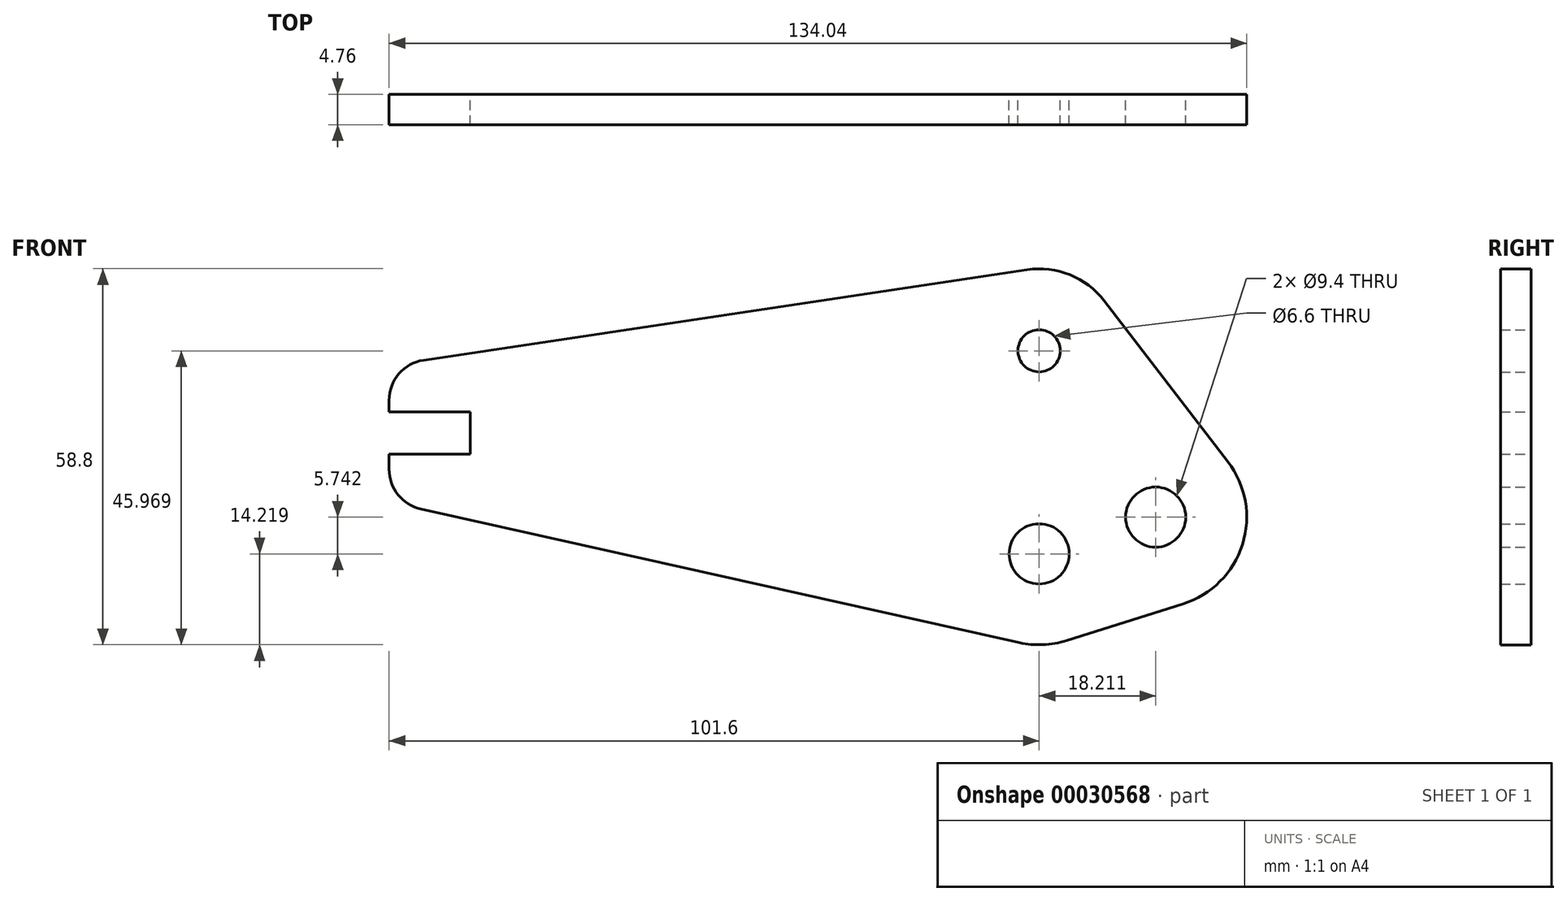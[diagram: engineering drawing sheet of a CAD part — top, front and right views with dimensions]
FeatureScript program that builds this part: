
annotation { "Feature Type Name" : "Feature", "Feature Type Description" : "" }
export const myFeature = defineFeature(function(context is Context, id is Id, definition is map)
    precondition{}
    {
        {
            var Q0;
            Q0=qCreatedBy(makeId("Front.planeOp"),FACE);
            var sketch = newSketch(context, id + "F0", { "sketchPlane" : qUnion([Q0])});
            skLineSegment(sketch, "E0", {"start": v(0, 10.3) * mm, "end": v(0, 12.7) * mm});
            skLineSegment(sketch, "E1", {"start": v(0, 12.7) * mm, "end": v(12.7, 12.7) * mm});
            skLineSegment(sketch, "E2", {"start": v(12.7, 12.7) * mm, "end": v(12.7, 19.3) * mm});
            skLineSegment(sketch, "E3", {"start": v(12.7, 19.3) * mm, "end": v(0, 19.3) * mm});
            skCircle(sketch, "E4", {"center": v(101.6, 28.83) * mm, "radius": 3.3 * mm});
            skArc(sketch, "E5.0", {"start": v(111.77, 36.64) * mm, "mid": v(106.4, 40.72) * mm, "end": v(99.7, 41.51) * mm});
            skLineSegment(sketch, "E6", {"start": v(0, 19.3) * mm, "end": v(0, 21.08) * mm});
            skLineSegment(sketch, "E7", {"start": v(5.4, 27.36) * mm, "end": v(99.7, 41.51) * mm});
            skLineSegment(sketch, "E8", {"start": v(101.6, 28.83) * mm, "end": v(101.6, -2.92) * mm, "construction": true});
            skLineSegment(sketch, "E9", {"start": v(101.6, 28.83) * mm, "end": v(119.81, 2.82) * mm, "construction": true});
            skCircle(sketch, "E10", {"center": v(101.6, -2.92) * mm, "radius": 4.7 * mm});
            skCircle(sketch, "E11", {"center": v(119.81, 2.82) * mm, "radius": 4.7 * mm});
            skArc(sketch, "E12.0", {"start": v(98.5, -16.8) * mm, "mid": v(102.2, -17.13) * mm, "end": v(105.88, -16.49) * mm});
            skArc(sketch, "E13.0", {"start": v(124.09, -10.74) * mm, "mid": v(133.38, -1.45) * mm, "end": v(131.1, 11.48) * mm});
            skLineSegment(sketch, "E14", {"start": v(4.97, 4.1) * mm, "end": v(98.5, -16.8) * mm});
            skLineSegment(sketch, "E15", {"start": v(111.77, 36.64) * mm, "end": v(131.1, 11.48) * mm});
            skLineSegment(sketch, "E16", {"start": v(105.88, -16.49) * mm, "end": v(124.09, -10.74) * mm});
            skArc(sketch, "E17.trimOffspring", {"start": v(96.91, -2.57) * mm, "mid": v(111.15, -1.45) * mm, "end": v(123.45, 5.8) * mm, "construction": true});
            skPoint(sketch, "E18.visualSharp", {"position": v(0, 26.55) * mm});
            skArc(sketch, "E18.filletArc", {"start": v(5.4, 27.36) * mm, "mid": v(1.54, 25.23) * mm, "end": v(0, 21.08) * mm});
            skPoint(sketch, "E19.visualSharp", {"position": v(0, 5.2) * mm});
            skArc(sketch, "E19.filletArc", {"start": v(0, 10.3) * mm, "mid": v(1.4, 6.32) * mm, "end": v(4.97, 4.1) * mm});
            skSolve(sketch);
        }
        {
            var Q0;
            Q0=makeQuery(id+"F0.imprint","IMPRINT",FACE,{"disambiguationData":[TD([[makeQuery(id+"F0.imprint","IMPRINT",EDGE,{"derivedFrom":sQuery(id+"F0.wireOp",EDGE,"E0")}),-1.0]])]});
            extrude(context, id + "F1", {"entities" : qUnion([Q0]), "depth" : 4.76 * mm});
        }
    });
